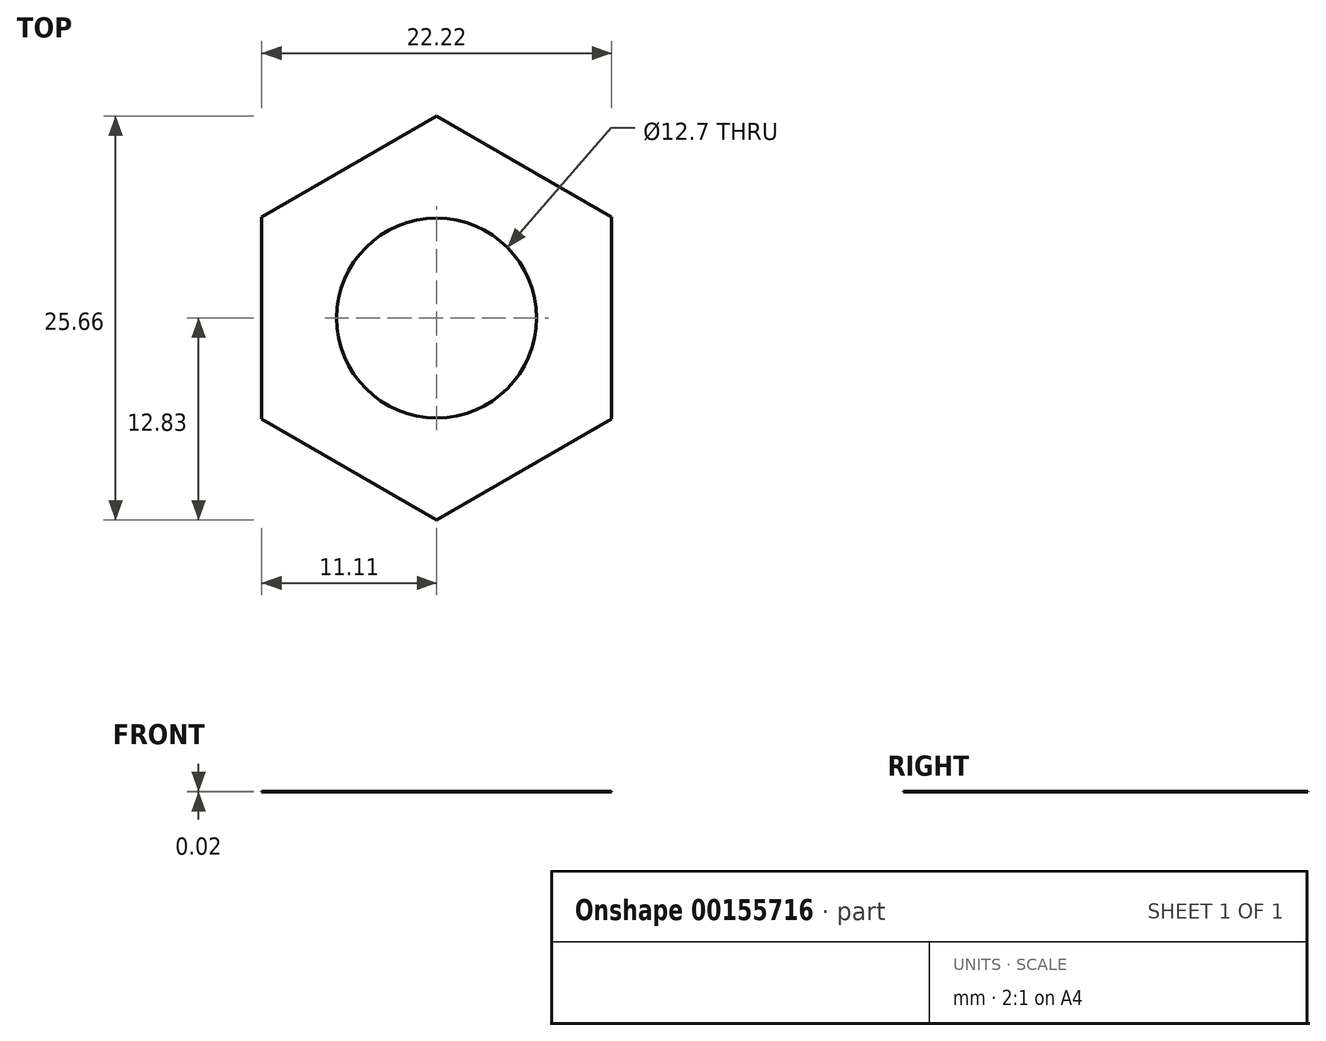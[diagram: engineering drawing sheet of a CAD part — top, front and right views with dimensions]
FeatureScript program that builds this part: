
annotation { "Feature Type Name" : "Feature", "Feature Type Description" : "" }
export const myFeature = defineFeature(function(context is Context, id is Id, definition is map)
    precondition{}
    {
        {
            var Q0;
            Q0=qCreatedBy(makeId("Top.planeOp"),FACE);
            var sketch = newSketch(context, id + "F2", { "sketchPlane" : qUnion([Q0])});
            skCircle(sketch, "E0.cCircle", {"center": v(0, 0) * mm, "radius": 11.11 * mm, "construction": true});
            skLineSegment(sketch, "E0.0", {"start": v(11.11, 6.42) * mm, "end": v(11.11, -6.42) * mm});
            skLineSegment(sketch, "E0.1", {"start": v(11.11, -6.42) * mm, "end": v(0, -12.83) * mm});
            skLineSegment(sketch, "E0.2", {"start": v(0, -12.83) * mm, "end": v(-11.11, -6.42) * mm});
            skLineSegment(sketch, "E0.3", {"start": v(-11.11, -6.42) * mm, "end": v(-11.11, 6.42) * mm});
            skLineSegment(sketch, "E0.4", {"start": v(-11.11, 6.42) * mm, "end": v(0, 12.83) * mm});
            skLineSegment(sketch, "E0.5", {"start": v(0, 12.83) * mm, "end": v(11.11, 6.42) * mm});
            skPoint(sketch, "E0.0.midPoint", {"position": v(11.11, 0) * mm});
            skCircle(sketch, "E1", {"center": v(0, 0) * mm, "radius": 6.35 * mm});
            skSolve(sketch);
        }
        {
            var Q0;
            Q0 = qSketchRegion(id + "F2", true);
            extrude(context, id + "F0", {"entities" : qUnion([Q0]), "endBound" : BoundingType.SYMMETRIC, "depth" : 7 / 406.4 * mm});
        }
        {
            var Q0;
            Q0=qCreatedBy(makeId("Front.planeOp"),FACE);
            var sketch = newSketch(context, id + "F3", { "sketchPlane" : qUnion([Q0])});
            skLineSegment(sketch, "E2", {"start": v(0, 7.51) * mm, "end": v(0, -7.32) * mm, "construction": true});
            skLineSegment(sketch, "E3", {"start": v(14.5, 5.56) * mm, "end": v(14.5, 3.6) * mm});
            skLineSegment(sketch, "E4", {"start": v(14.5, 5.56) * mm, "end": v(11.11, 5.56) * mm});
            skLineSegment(sketch, "E5", {"start": v(11.11, 5.56) * mm, "end": v(14.5, 3.6) * mm});
            skSolve(sketch);
        }
        {
            var Q0;
            Q0 = qSketchRegion(id + "F3", true);
            var Q1;
            Q1=sQuery(id+"F3.wireOp",EDGE,"E2");
            revolve(context, id + "F1", {"operationType" : NewBodyOperationType.REMOVE, "entities" : qUnion([Q0]), "axis" : qUnion([Q1]), "revolveType" : RevolveType.FULL, "oppositeDirection" : true});
        }
    });
